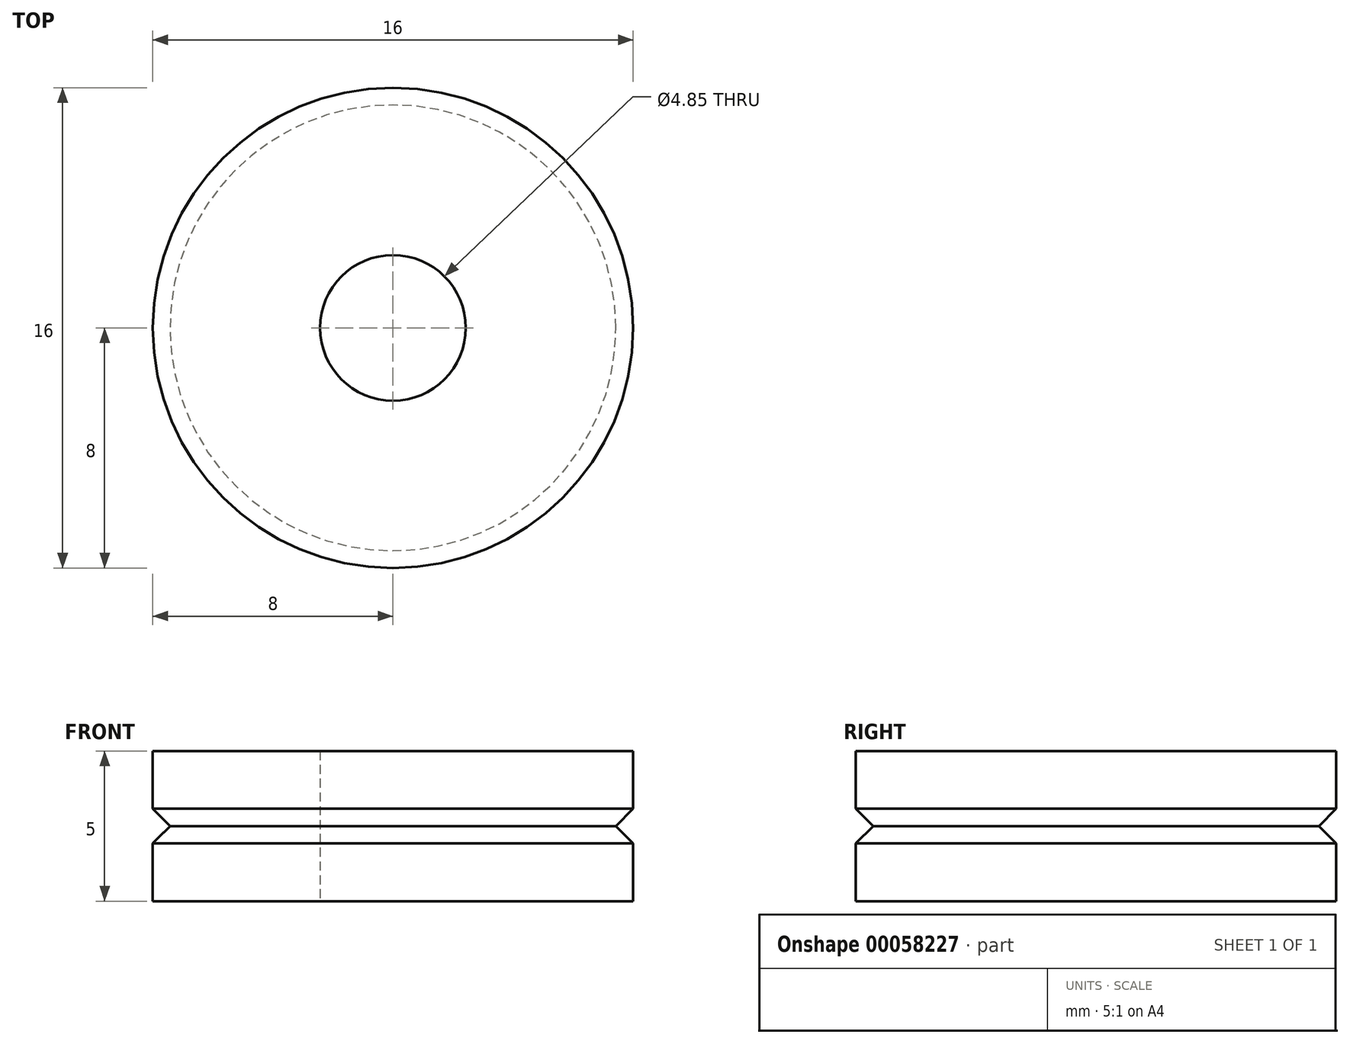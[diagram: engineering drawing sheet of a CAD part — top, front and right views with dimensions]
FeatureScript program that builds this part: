
annotation { "Feature Type Name" : "Feature", "Feature Type Description" : "" }
export const myFeature = defineFeature(function(context is Context, id is Id, definition is map)
    precondition{}
    {
        {
            var Q0;
            Q0=qCreatedBy(makeId("Front.planeOp"),FACE);
            var sketch = newSketch(context, id + "F0", { "sketchPlane" : qUnion([Q0])});
            skLineSegment(sketch, "E0", {"start": v(0, 0) * mm, "end": v(0, 4.14) * mm, "construction": true});
            skLineSegment(sketch, "E1", {"start": v(8, 0) * mm, "end": v(8, 1.92) * mm});
            skLineSegment(sketch, "E2", {"start": v(8, 1.92) * mm, "end": v(7.42, 2.5) * mm});
            skLineSegment(sketch, "E3", {"start": v(7.42, 2.5) * mm, "end": v(0, 2.5) * mm, "construction": true});
            skLineSegment(sketch, "E4.MirrorCS", {"start": v(8, 3.07) * mm, "end": v(7.42, 2.5) * mm});
            skLineSegment(sketch, "E5.MirrorCS", {"start": v(8, 5) * mm, "end": v(8, 3.08) * mm});
            skLineSegment(sketch, "E6", {"start": v(8, 0) * mm, "end": v(2.43, 0) * mm});
            skLineSegment(sketch, "E7", {"start": v(2.43, 0) * mm, "end": v(2.43, 5) * mm});
            skLineSegment(sketch, "E8", {"start": v(2.42, 5) * mm, "end": v(8, 5) * mm});
            skSolve(sketch);
        }
        {
            var Q0;
            Q0 = qSketchRegion(id + "F0", true);
            var Q1;
            Q1=sQuery(id+"F0.wireOp",EDGE,"E0");
            revolve(context, id + "F1", {"entities" : qUnion([Q0]), "axis" : qUnion([Q1]), "revolveType" : RevolveType.FULL});
        }
    });
